# Revit family: Legrand_ElectricFireStopping_EZPathFirestopModule_Series33_Floor
name_source: partatom
category: Equipement spécialisé
units: mm (PartAtom-declared; Revit-internal decimal feet)

## family parameters
Cote de connecteur circulaire = Utiliser le diamètre
Couper avec des vides une fois chargée = Non
Hôte = Sol
Numéro OmniClass = 23.20.50.14
Partagée = Non
Point de calcul de pièce = Non
Titre OmniClass = Firestopping
Toujours verticalement = Oui
Type d'élément = Normal

## types (1)
- 1 Device with Circular Plate Réf 250018 + 250220
    AirLeakage(UL1479) = 0.14 m3/h 0% cable, 1.14 m3/h 100% cable
    AssetType = Fixed
    BIMObjectName = Legrand_ElectricFireStopping_EZPathFirestopModule_Series33_Floor_1DeviceCircularPlate
    Classification(EN13501-2) = EI 120
    ClassificationName = Uniclass2015
    ClassificationValue = Ss_25_60_30
    Code d'assemblage = D4030900
    CodePerformance = Conforms to the European standard EN1366-3, BS476/20, ASTM E814 and DIN4102-9
    Color = Red
    Commentaires du type = 1 Device with Circular Plate
    Description = EZ-Path is a mechanical device that provides fully compliant fire stopping for power and data cable management pathways.
    DocumentationInstallationGuide = https://www.legrand.co.uk
    DocumentationLiterature = https://specifi.bimstore.co.uk
    DocumentationMaintenance = https://www.legrand.co.uk
    DocumentationTechnical = https://www.legrand.co.uk
    DurationUnit = Years
    EZ path 1 = Oui
    EZ path 2 = Non
    EZ path 3 = Non
    EZ path 4 = Non
    EZ path 5 = Non
    EZ path 6 = Non
    EZ path 7 = Non
    EZPathCutoutHeight = 50 mm
    EZPathCutoutWidth = 68 mm
    EZPathDevice = Firestop-STI-EZ_Path-Series_33_Fire_Rated_Pathway
    EZPathHeight = 75 mm
    EZPathLeftCenterOfGanged = 38 mm
    EZPathWidth = 75 mm
    Elévation par défaut = 0 mm  [stored 0 ft]
    ExpansionBegins = 177 deg C
    ExpectedLife = 0
    Fabricant = Legrand Electric Ltd
    Features = The modules, which are suitable for all types of wall, can be assembled and installed horizontally or vertically to form a sturdy unit
    Finish = Powder Coated
    FireRating = Up to 4 Hr
    FireResistance(EN1366-3) = 2 Hours
    FloorCutoutHeight = 78 mm
    FloorCutoutWidth = 78 mm
    FloorLeftCutoutCenterWidth = 39 mm
    General Conditions of Use = https://export.legrand.com
    IfcExportAs = IfcBuildingElementPart
    IfcExportType = IfcBuildingElementPartTypeEnum.FIRESTOP
    InServiceTemperature = Not to exceed 49 deg C
    ManufacturerName = Legrand Electric Ltd
    Material = 1.5mm thk Galv Steel
    ModelNumber = CM250018
    ModelNumberBrackets = CM250220
    ModelNumberDevice = CM250018
    ModelNumberExtensions = CM250078
    ModelReference = EZ-Path® Permanent Automatic Mechanical Firestop System (Series 33) Floor
    Modèle = EZ-Path® Permanent Automatic Mechanical Firestop System (Series 33) Floor
    MountingPlateCutoutHeight = 76 mm
    MountingPlateCutoutWidth = 76 mm
    MountingPlateHeight = 102 mm
    MountingPlateHeightCenterline = 1524 mm  [stored 5 ft]
    MountingPlateLeftCenterWidth = 51 mm
    MountingPlateLeftCutoutCenterWidth = 38 mm
    MountingPlateWidth = 102 mm
    MountingPlateWidthCenterline = 1524 mm  [stored 5 ft]
    NBSDescription = Fire stopping systems
    NBSObjectName = Legrand Electric Ltd - Fire stopping systems
    NBSReference = 30-85-30
    NoGanged = 1
    NoOfDevices = 1
    NoPlate = Non
    NominalHeight = 78 mm
    NominalWidth = 78 mm
    Note d'identification = P12
    PlateType = 3
    ProductPage = https://www.legrand.co.uk
    ProductionYear = 2017
    ReactionToFire(EN13501-1) = Class E
    ReferencedStandard = CE Marking, EN 1366-3, ETA 130993
    Region = Europe
    RetainingPlate = Firestop-STI-EZ_Path-Retaining_Plate
    RoundPlateBottomHeightCenterline = 0 mm  [stored 0 ft]
    RoundPlateBottomOfFloor = Oui
    RoundPlateBottomWidthCenterline = 0 mm  [stored 0 ft]
    RoundPlateCutoutHeight = 76 mm
    RoundPlateCutoutWidth = 76 mm
    RoundPlateDia = 127 mm
    RoundPlateTopOfFloor = Non
    RoundPlateTopWidthCenterline = 1524 mm  [stored 5 ft]
    RoundPlatetopHeightCenterline = 1524 mm  [stored 5 ft]
    SafetyDataSheet = https://files.stifirestop.com
    SecondaryModelNumberBrackets = EZP133KT
    SecondaryModelNumberDevice = EZD33T
    SecondaryModelNumberExtensions = EZD33E
    Shape = Square (Series 33)
    ShelfLife = No Limit
    Size = 80x80mm
    SoundInsulation(ASTME90) = STC 50
    SquarePlate = Non
    TestedSystems = https://www.legrand.co.uk
    TypeName = 1 Device with Circular Plate
    URL = https://www.legrand.co.uk
    VolumeExpansion = 800%
    WarrantyDescription = Firestop certification guaranteed throughout the entire lifetime of the electrical installation
    WarrantyDurationLabor = 0
    WarrantyDurationParts = 0
    WarrantyDurationUnit = Years
    Weight(Kg) = 1.16 kg
    _BSBibleVersion = 15
    _BimSpecGuid = 0
    _CurrentRevision = 2
    _DistributedBy = www.bimstore.co.uk

note: [stored X ft] marks values corroborated as IEEE doubles in the binary element streams (Revit-internal decimal feet)

## geometry (parser evidence)
native form markers: Blend x6, Sweep x7
no freeform markers — native parametric forms only
